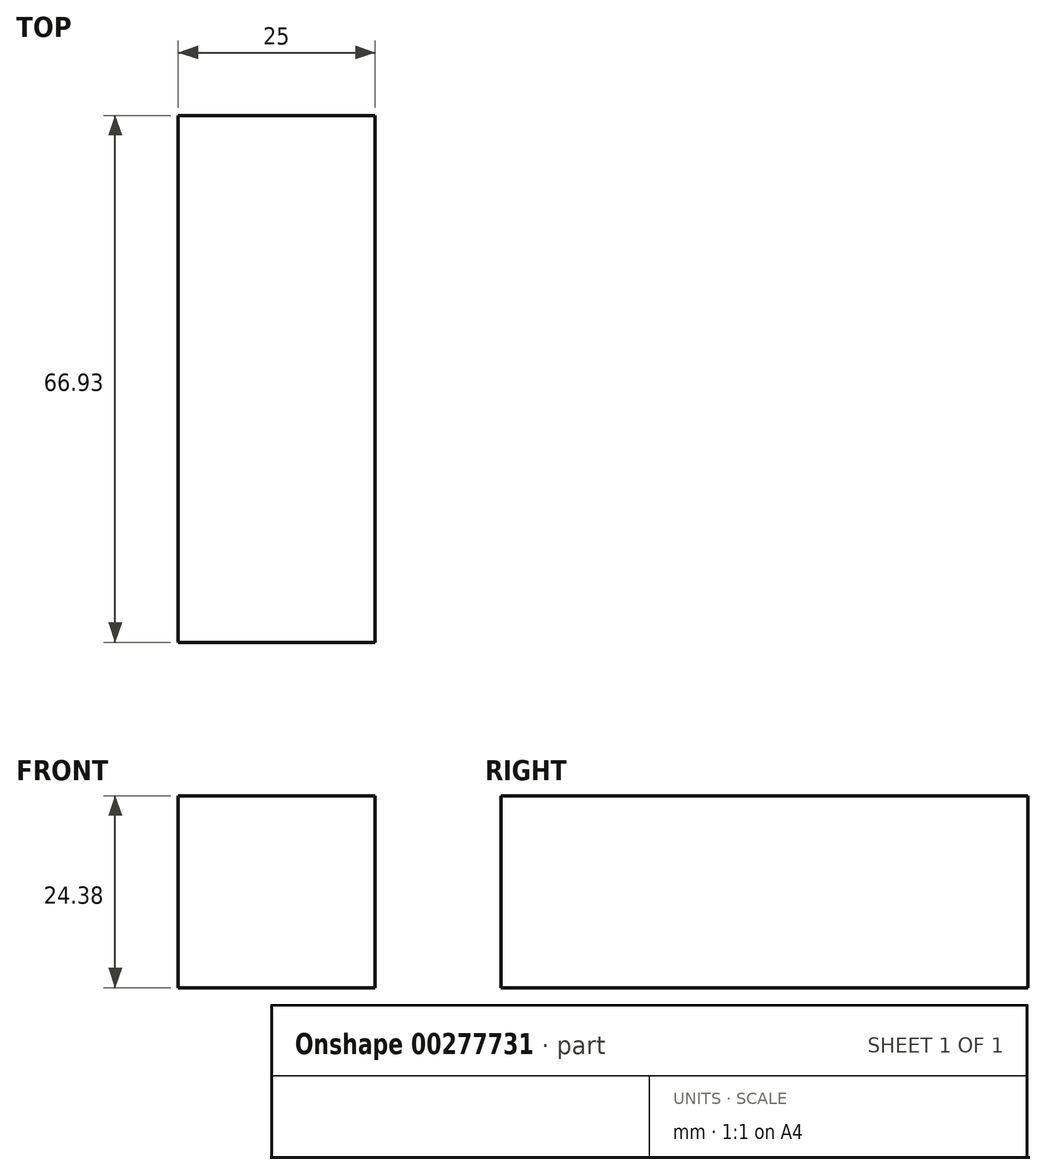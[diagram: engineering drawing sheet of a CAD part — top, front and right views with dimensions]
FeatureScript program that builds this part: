
annotation { "Feature Type Name" : "Feature", "Feature Type Description" : "" }
export const myFeature = defineFeature(function(context is Context, id is Id, definition is map)
    precondition{}
    {
        {
            var Q0;
            Q0=qCreatedBy(makeId("Front.planeOp"),FACE);
            var sketch = newSketch(context, id + "F0", { "sketchPlane" : qUnion([Q0])});
            skLineSegment(sketch, "E0", {"start": v(-44.97, 40.76) * mm, "end": v(-58.46, -24.45) * mm});
            skSolve(sketch);
        }
        {
            var Q0;
            Q0 = qSketchRegion(id + "F0", true);
            var Q1;
            Q1=sQuery(id+"F0.wireOp",EDGE,"E0");
            extrude(context, id + "F1", {"entities" : qUnion([Q0]), "bodyType" : ToolBodyType.SURFACE, "surfaceEntities" : qUnion([Q1]), "depth" : 40.9 * mm});
        }
        {
            var Q0;
            Q0=qCreatedBy(makeId("Right.planeOp"),FACE);
            var sketch = newSketch(context, id + "F2", { "sketchPlane" : qUnion([Q0])});
            skLineSegment(sketch, "E1.bottom", {"start": v(108.74, 40.09) * mm, "end": v(41.81, 40.09) * mm});
            skLineSegment(sketch, "E1.top", {"start": v(108.74, 15.71) * mm, "end": v(41.81, 15.71) * mm});
            skLineSegment(sketch, "E1.left", {"start": v(108.74, 40.09) * mm, "end": v(108.74, 15.71) * mm});
            skLineSegment(sketch, "E1.right", {"start": v(41.81, 40.09) * mm, "end": v(41.81, 15.71) * mm});
            skSolve(sketch);
        }
        {
            var Q0;
            Q0 = qSketchRegion(id + "F2", true);
            extrude(context, id + "F3", {"entities" : qUnion([Q0]), "depth" : 25 * mm});
        }
    });
